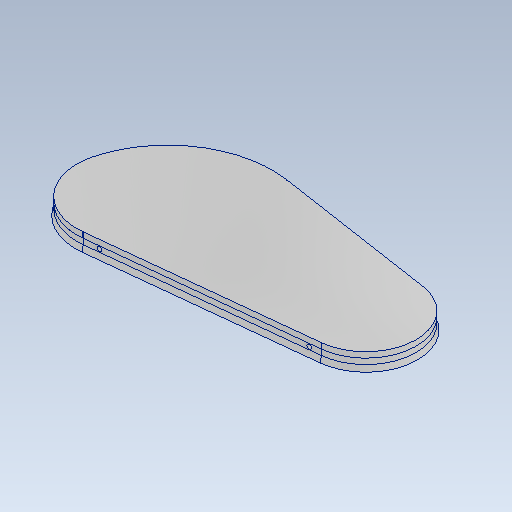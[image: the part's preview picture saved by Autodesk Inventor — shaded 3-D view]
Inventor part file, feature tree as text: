
AUTODESK INVENTOR PART (.ipt)
format: ipt  version: 2021 (Build 250183000, 183)  size: 221,184 bytes
history: native  units: mm
features: sketch x9, other x5
ambient origin geometry x8: Origin, YZ Plane, XZ Plane, XY Plane, X Axis, Y Axis, Z Axis, Center Point
bodies: Solid1 (feature_tree), Solid2 (feature_tree), Solid3 (feature_tree)
feature tree (14):
  other  "Shoes (Lower part).ipt"
  other  "Solid1::Shoes (Lower part).ipt"
  other  "Solid2::Shoes (Lower part).ipt"
  other  "Solid3::Shoes (Lower part).ipt"
  other  "TaggingFeature1"
  sketch  "Sketch1"  dims[d0=10.0mm]
  sketch  "Sketch2"
  sketch  "Sketch3"
  sketch  "Sketch4"
  sketch  "Sketch5"
  sketch  "Sketch6"
  sketch  "Sketch7"
  sketch  "Sketch8"
  sketch  "Sketch9"
